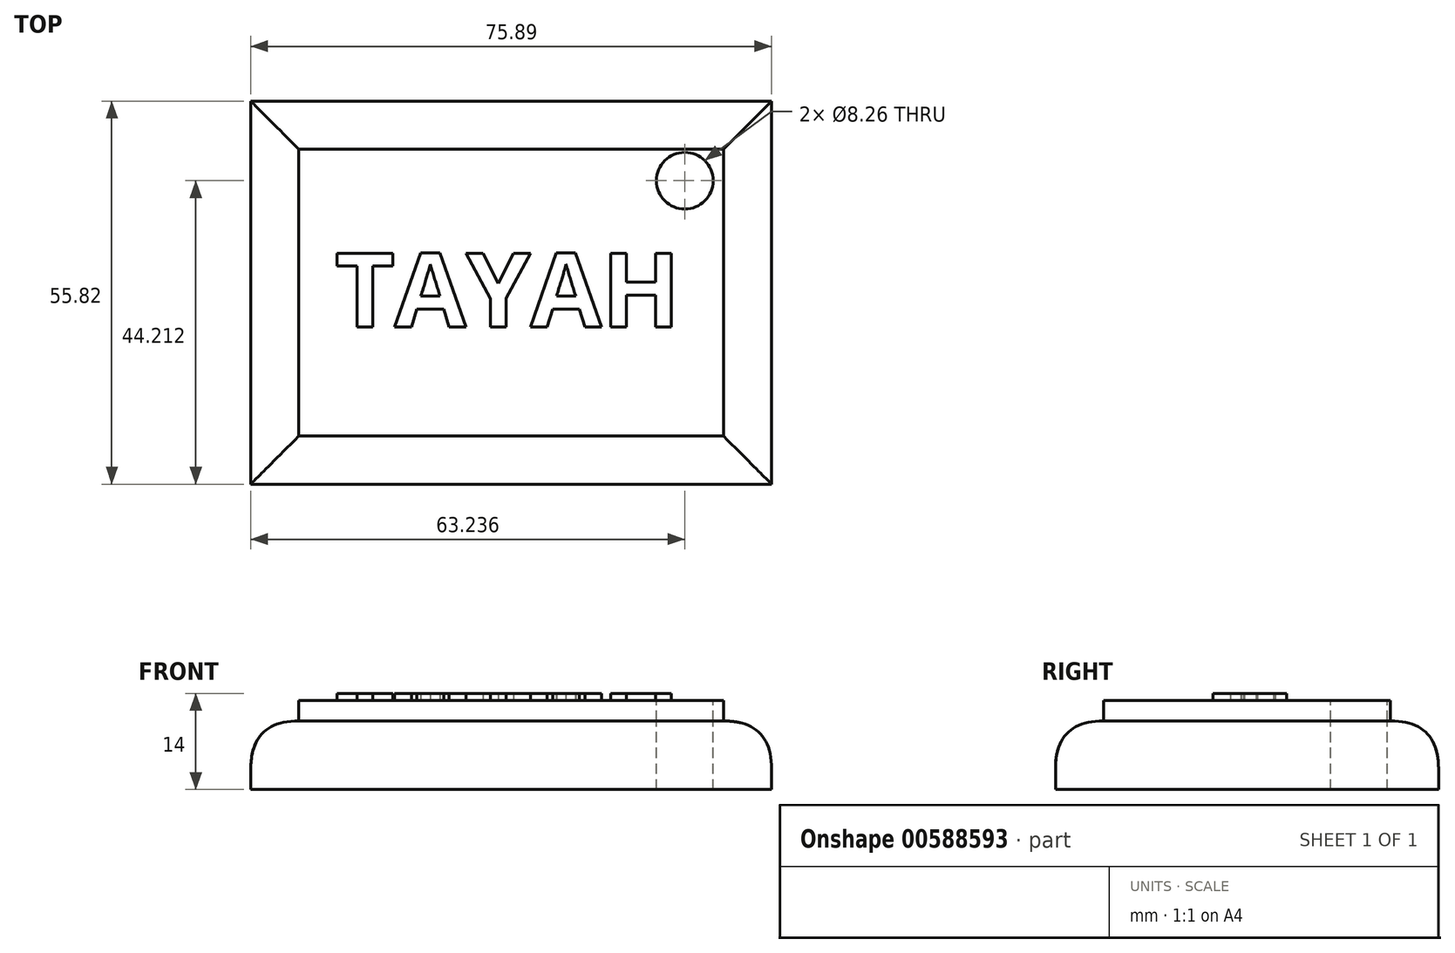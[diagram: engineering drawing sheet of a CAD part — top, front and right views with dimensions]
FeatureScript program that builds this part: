
annotation { "Feature Type Name" : "Feature", "Feature Type Description" : "" }
export const myFeature = defineFeature(function(context is Context, id is Id, definition is map)
    precondition{}
    {
        {
            var Q0;
            Q0=qCreatedBy(makeId("Top.planeOp"),FACE);
            var sketch = newSketch(context, id + "F0", { "sketchPlane" : qUnion([Q0])});
            skLineSegment(sketch, "E0.bottom", {"start": v(0, 0) * mm, "end": v(-75.89, 0) * mm});
            skLineSegment(sketch, "E0.top", {"start": v(0, 55.82) * mm, "end": v(-75.89, 55.82) * mm});
            skLineSegment(sketch, "E0.left", {"start": v(0, 0) * mm, "end": v(0, 55.82) * mm});
            skLineSegment(sketch, "E0.right", {"start": v(-75.89, 0) * mm, "end": v(-75.89, 55.82) * mm});
            skSolve(sketch);
        }
        {
            var Q0;
            Q0 = qSketchRegion(id + "F0", true);
            extrude(context, id + "F1", {"entities" : qUnion([Q0]), "depth" : 10 * mm, "offsetDistance" : 25.4 * mm});
        }
        {
            var Q0;
            Q0=makeQuery(id+"F1.opExtrude","CAP_FACE",FACE,{"disambiguationData":[OSD([sQuery(id+"F0.wireOp",EDGE,"E0.bottom"),sQuery(id+"F0.wireOp",EDGE,"E0.top"),sQuery(id+"F0.wireOp",EDGE,"E0.left"),sQuery(id+"F0.wireOp",EDGE,"E0.right")])],"isStart":false});
            fillet(context, id + "F2", {"entities" : qUnion([Q0]), "radius" : 7 * mm, "tangentPropagation" : true, "rho" : 0.5, "crossSection" : FilletCrossSection.CONIC, "allowEdgeOverflow" : false});
        }
        {
            var Q0;
            Q0=makeQuery(id+"F1.opExtrude","CAP_FACE",FACE,{"disambiguationData":[OSD([sQuery(id+"F0.wireOp",EDGE,"E0.bottom"),sQuery(id+"F0.wireOp",EDGE,"E0.top"),sQuery(id+"F0.wireOp",EDGE,"E0.left"),sQuery(id+"F0.wireOp",EDGE,"E0.right")])],"isStart":false});
            extrude(context, id + "F3", {"entities" : qUnion([Q0]), "depth" : 3 * mm, "offsetDistance" : 25 * mm});
        }
        {
            var Q0;
            Q0=makeQuery(id+"F3.opExtrude","CAP_FACE",FACE,{"disambiguationData":[OSD([sQuery(id+"F0.wireOp",EDGE,"E0.bottom"),sQuery(id+"F0.wireOp",EDGE,"E0.top"),sQuery(id+"F0.wireOp",EDGE,"E0.left"),sQuery(id+"F0.wireOp",EDGE,"E0.right")])],"isStart":false});
            var sketch = newSketch(context, id + "F4", { "sketchPlane" : qUnion([Q0])});
            skText(sketch, "E1", { "text": "TAYAH", "fontName": "OpenSans-Bold.ttf"});
            const initialGuessF4  = {"E1": [-0.06362, 0.02292, 1, 0, 0.01083]};
            skSetInitialGuess(sketch, initialGuessF4);
            skSolve(sketch);
        }
        {
            var Q0;
            Q0=makeQuery(id+"F4.imprint","IMPRINT",FACE,{"disambiguationData":[TD([[makeQuery(id+"F4.imprint","IMPRINT",EDGE,{"derivedFrom":sQuery(id+"F4.wireOp",EDGE,"E1.sketch_text.stroke-0")}),1.0]])]});
            var sketch = newSketch(context, id + "F5", { "sketchPlane" : qUnion([Q0])});
            skCircle(sketch, "E2", {"center": v(-12.65, 44.21) * mm, "radius": 4.13 * mm});
            skSolve(sketch);
        }
        {
            var Q0;
            Q0 = qSketchRegion(id + "F4", true);
            extrude(context, id + "F6", {"entities" : qUnion([Q0]), "operationType" : NewBodyOperationType.ADD, "depth" : 1 * mm, "offsetDistance" : 25 * mm});
        }
        {
            var Q0;
            Q0=makeQuery(id+"F5.imprint","IMPRINT",FACE,{"disambiguationData":[TD([[makeQuery(id+"F5.imprint","IMPRINT",EDGE,{"derivedFrom":sQuery(id+"F5.wireOp",EDGE,"E2")}),1.0]])]});
            extrude(context, id + "F7", {"entities" : qUnion([Q0]), "operationType" : NewBodyOperationType.REMOVE, "oppositeDirection" : true, "depth" : 29.6 * mm, "offsetDistance" : 25 * mm});
        }
    });
